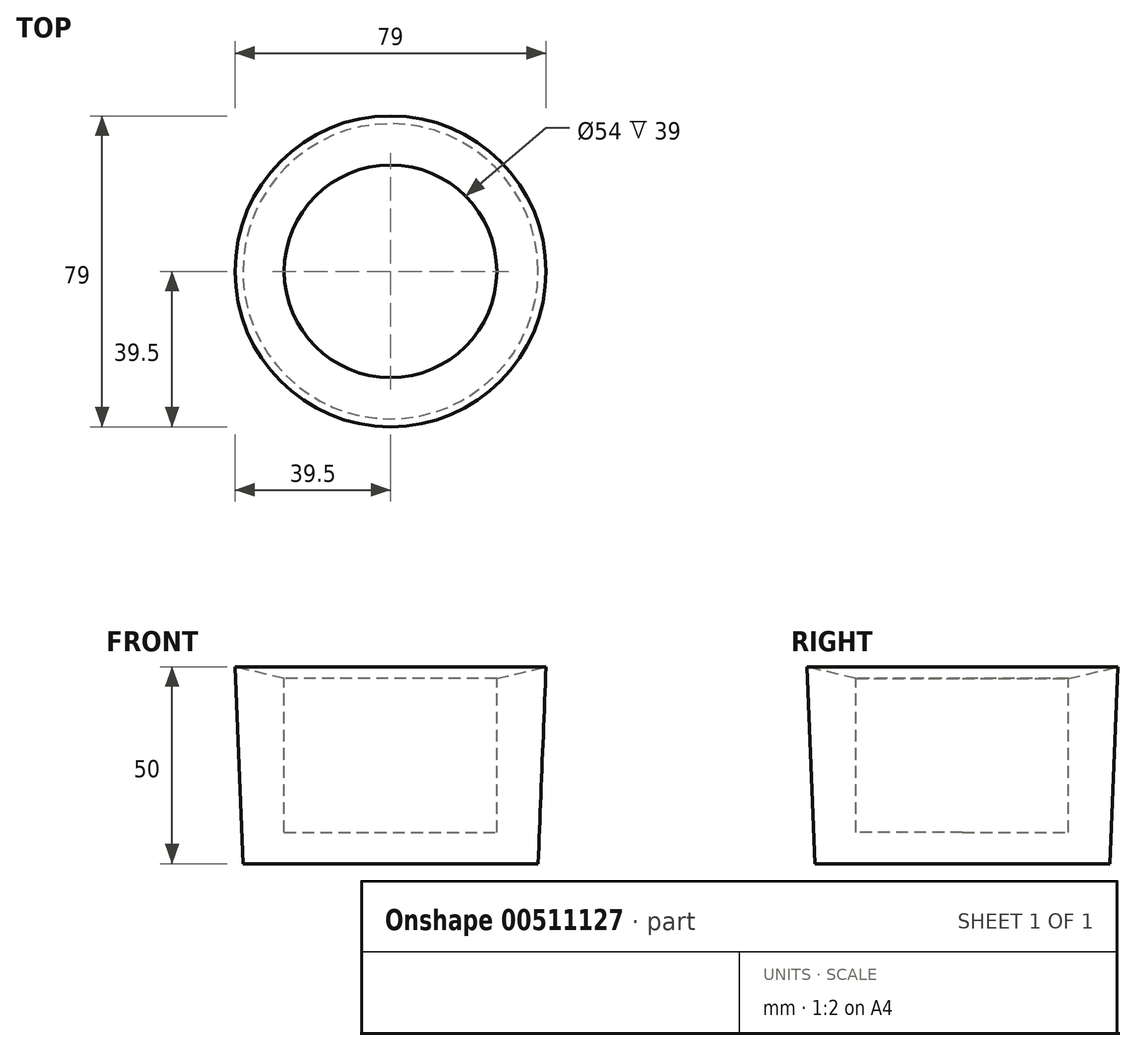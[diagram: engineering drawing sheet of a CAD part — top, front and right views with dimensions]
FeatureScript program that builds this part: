
annotation { "Feature Type Name" : "Feature", "Feature Type Description" : "" }
export const myFeature = defineFeature(function(context is Context, id is Id, definition is map)
    precondition{}
    {
        {
            var Q0;
            Q0=qCreatedBy(makeId("Right.planeOp"),FACE);
            var sketch = newSketch(context, id + "F0", { "sketchPlane" : qUnion([Q0])});
            skLineSegment(sketch, "E0", {"start": v(-39.5, 50) * mm, "end": v(-27, 47) * mm});
            skLineSegment(sketch, "E1", {"start": v(-27, 47) * mm, "end": v(-27, 3) * mm});
            skLineSegment(sketch, "E2", {"start": v(-27, 3) * mm, "end": v(0, 3) * mm});
            skLineSegment(sketch, "E3", {"start": v(0, 3) * mm, "end": v(0, 0) * mm});
            skLineSegment(sketch, "E4", {"start": v(0, 0) * mm, "end": v(-37.5, 0) * mm});
            skLineSegment(sketch, "E5", {"start": v(-37.5, 0) * mm, "end": v(-39.5, 50) * mm});
            skSolve(sketch);
        }
        {
            var Q0;
            Q0=makeQuery(id+"F0.imprint","IMPRINT",FACE,{"disambiguationData":[TD([[makeQuery(id+"F0.imprint","IMPRINT",EDGE,{"derivedFrom":sQuery(id+"F0.wireOp",EDGE,"E0")}),-1.0]])]});
            var Q1;
            Q1=sQuery(id+"F0.wireOp",EDGE,"E3");
            revolve(context, id + "F1", {"entities" : qUnion([Q0]), "axis" : qUnion([Q1]), "revolveType" : RevolveType.FULL});
        }
        {
            var Q0;
            Q0=makeQuery(id+"F1.opRevolve","SWEPT_FACE",FACE,{"disambiguationData":[OSD([sQuery(id+"F0.wireOp",EDGE,"E2")])]});
            extrude(context, id + "F2", {"entities" : qUnion([Q0]), "operationType" : NewBodyOperationType.ADD, "depth" : 5 * mm});
        }
    });
